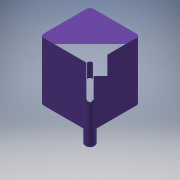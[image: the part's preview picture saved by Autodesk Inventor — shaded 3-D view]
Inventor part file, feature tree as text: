
AUTODESK INVENTOR PART (.ipt)
format: ipt  version: 2016 (Build 200138000, 138)  size: 136,704 bytes
history: native  units: mm
features: extrude x3, sketch x3, other x1, hole x1, chamfer x1, fillet x1
ambient origin geometry x8: Origin, YZ Plane, XZ Plane, XY Plane, X Axis, Y Axis, Z Axis, Center Point
bodies: Solid1 (feature_tree)
feature tree (10):
  other  "Fixture.ipt"
  extrude  "Extrusion1"  Depth=28.3mm
  hole  "Hole2"  [1 undecoded]
  sketch  "Sketch3"  dims[d3=51.0mm d4=0.0mm d12=2.0mm d13=0.0mm]
  extrude  "Extrusion2"  Depth=2.0mm TaperAngle=45.0deg
  extrude  "Extrusion3"  Depth=2.16mm
  chamfer  "Chamfer1"  Distance=10.0mm
  fillet  "Fillet1"  Radius=23.0mm
  sketch  "Sketch1"  dims[d0=28.3mm d2=22.0mm]
  sketch  "Sketch4"  dims[d15=20.0mm d16=0.0mm d17=0.6mm d18=2.0mm d19=45.0deg d20=2.16mm d21=10.0mm d22=23.0mm d23=2.5mm d24=6.0mm d25=4.0mm d26=2.0mm d27=90.0deg d28=8.0mm d29=20.594885mm d30=22.0mm d31=5.3mm]
note: 1 required parameter value undecoded (feature->parameter linkage not recoverable at this tier; creation-order binding heuristic only, values carry confidence <= 0.55)
